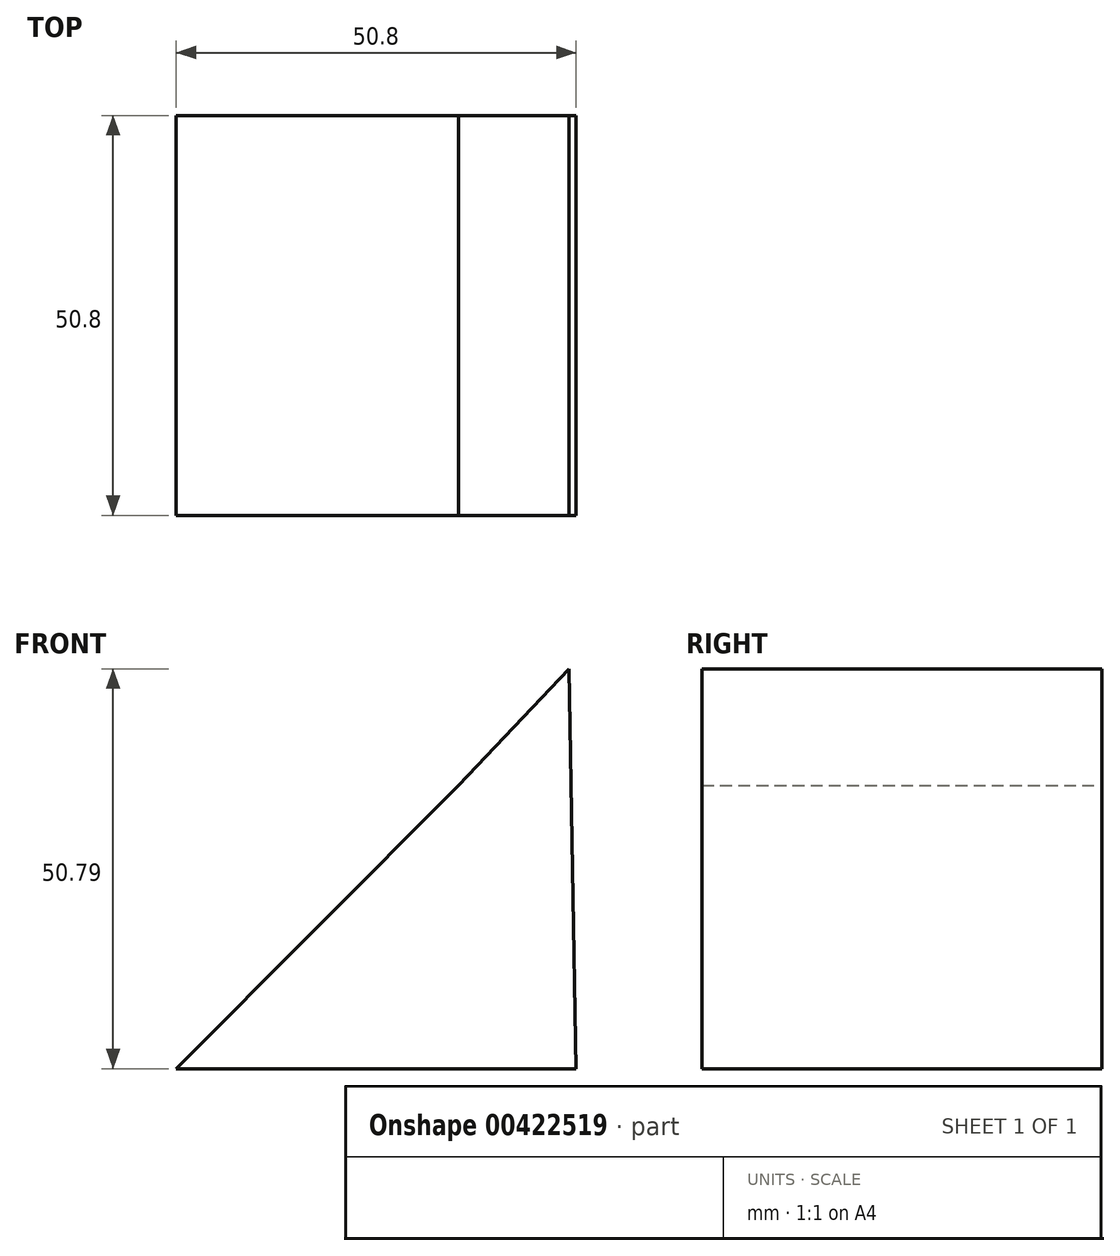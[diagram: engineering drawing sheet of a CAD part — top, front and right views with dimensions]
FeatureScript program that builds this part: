
annotation { "Feature Type Name" : "Feature", "Feature Type Description" : "" }
export const myFeature = defineFeature(function(context is Context, id is Id, definition is map)
    precondition{}
    {
        {
            var Q0;
            Q0=qCreatedBy(makeId("Front.planeOp"),FACE);
            var sketch = newSketch(context, id + "F0", { "sketchPlane" : qUnion([Q0])});
            skLineSegment(sketch, "E0", {"start": v(0, 0) * mm, "end": v(-49.89, 0) * mm});
            skLineSegment(sketch, "E1", {"start": v(-49.89, 0) * mm, "end": v(0.91, 0) * mm});
            skLineSegment(sketch, "E2", {"start": v(-49.89, 0) * mm, "end": v(-14.04, 36) * mm});
            skLineSegment(sketch, "E3", {"start": v(0.91, 0) * mm, "end": v(0, 50.8) * mm});
            skLineSegment(sketch, "E4", {"start": v(0, 50.8) * mm, "end": v(-14.04, 36) * mm});
            skSolve(sketch);
        }
        {
            var Q0;
            Q0 = qSketchRegion(id + "F0", true);
            extrude(context, id + "F1", {"entities" : qUnion([Q0]), "depth" : 50.8 * mm});
        }
    });
